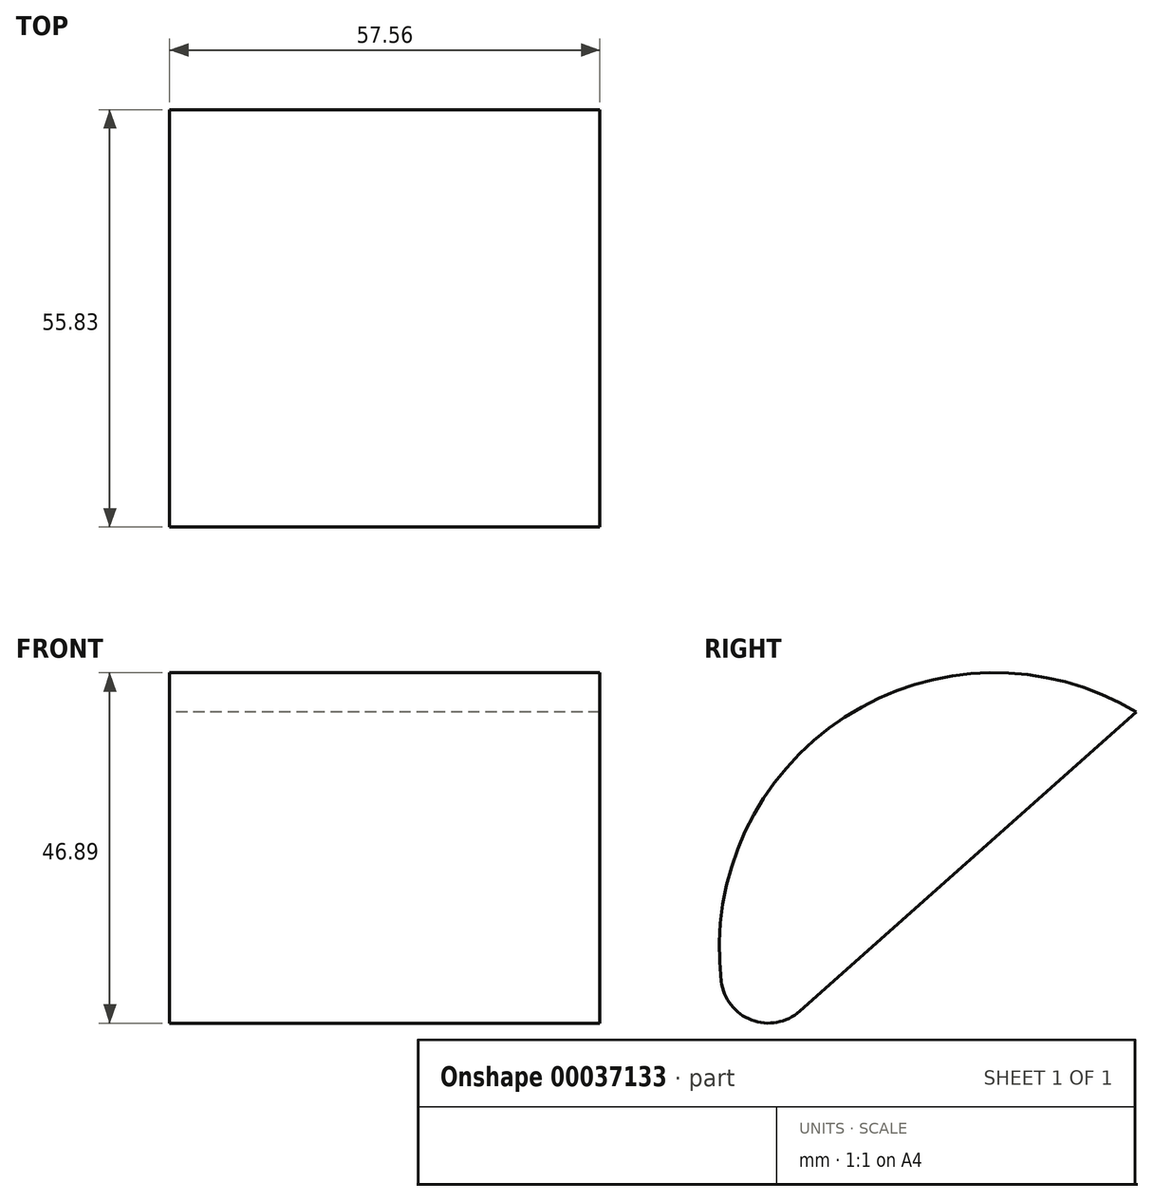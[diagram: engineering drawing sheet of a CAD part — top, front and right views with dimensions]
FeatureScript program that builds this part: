
annotation { "Feature Type Name" : "Feature", "Feature Type Description" : "" }
export const myFeature = defineFeature(function(context is Context, id is Id, definition is map)
    precondition{}
    {
        {
            var Q0;
            Q0=qCreatedBy(makeId("Right.planeOp"),FACE);
            var sketch = newSketch(context, id + "F0", { "sketchPlane" : qUnion([Q0])});
            skArc(sketch, "E0", {"start": v(0, 51.55) * mm, "mid": v(-39.03, 50.86) * mm, "end": v(-55.56, 15.5) * mm});
            skLineSegment(sketch, "E1", {"start": v(0, 51.55) * mm, "end": v(-45.04, 11.51) * mm});
            skPoint(sketch, "E2.visualSharp", {"position": v(-52.59, 4.8) * mm});
            skArc(sketch, "E2.filletArc", {"start": v(-55.56, 15.5) * mm, "mid": v(-51.5, 10.32) * mm, "end": v(-45.04, 11.51) * mm});
            skSolve(sketch);
        }
        {
            var Q0;
            Q0 = qSketchRegion(id + "F0", true);
            extrude(context, id + "F1", {"entities" : qUnion([Q0]), "depth" : 57.56 * mm});
        }
    });
